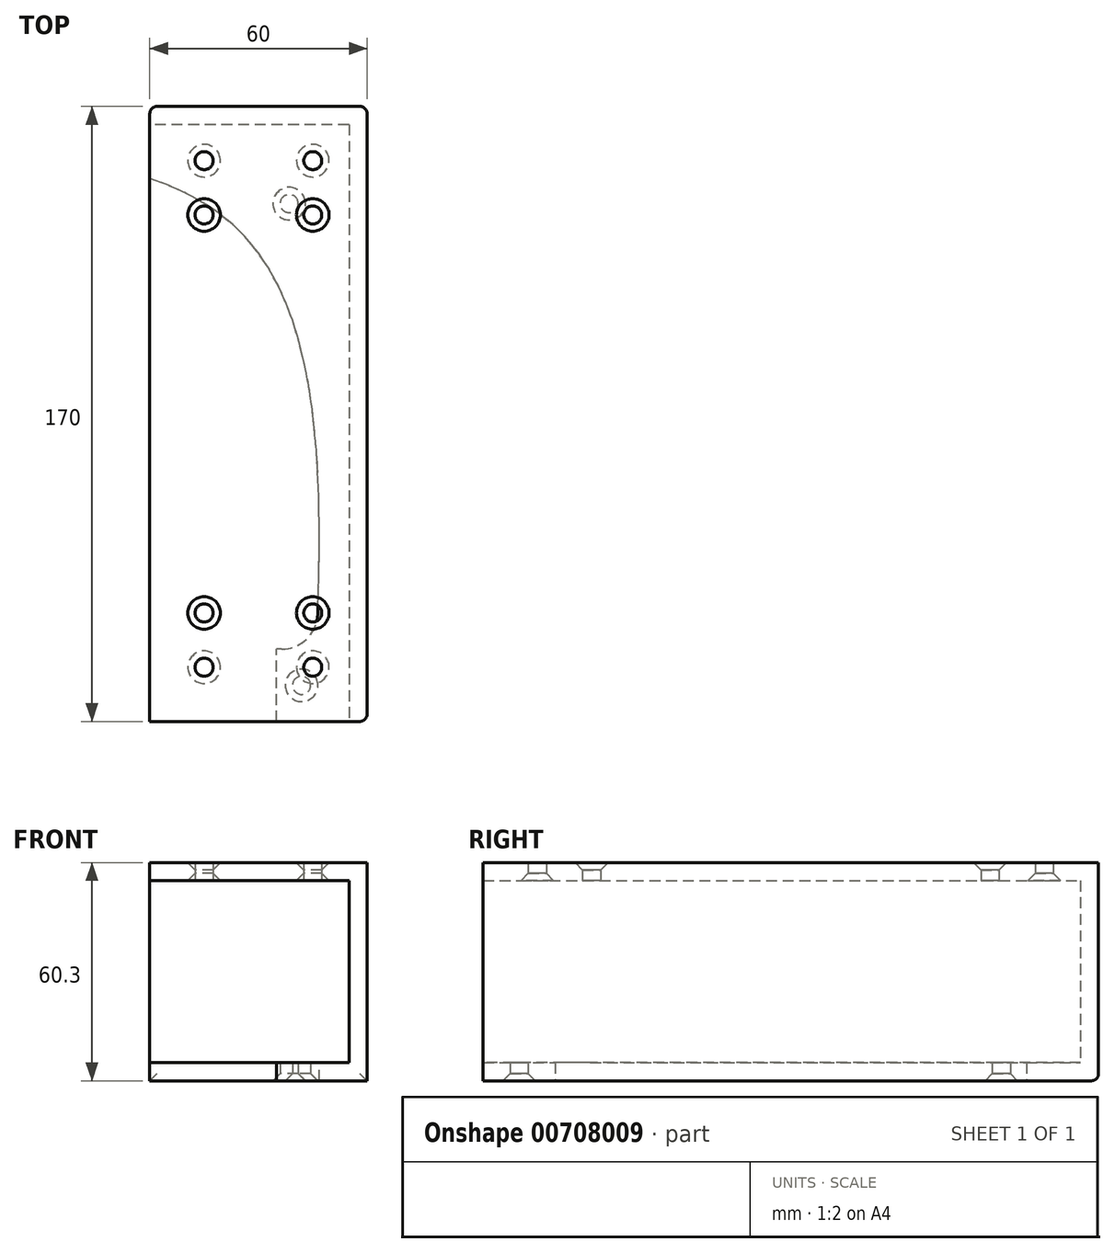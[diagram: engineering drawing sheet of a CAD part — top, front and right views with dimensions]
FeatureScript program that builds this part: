
annotation { "Feature Type Name" : "Feature", "Feature Type Description" : "" }
export const myFeature = defineFeature(function(context is Context, id is Id, definition is map)
    precondition{}
    {
        {
            var Q0;
            Q0=qCreatedBy(makeId("Top.planeOp"),FACE);
            var sketch = newSketch(context, id + "F0", { "sketchPlane" : qUnion([Q0])});
            skLineSegment(sketch, "E0.bottom", {"start": v(0, 0) * mm, "end": v(-60, 0) * mm});
            skLineSegment(sketch, "E0.top", {"start": v(0, 170) * mm, "end": v(-15, 170) * mm});
            skLineSegment(sketch, "E0.left", {"start": v(0, 0) * mm, "end": v(0, 170) * mm});
            skFitSpline(sketch, "E1", {"points": [v(-15, 170) * mm, v(-35.25, 34.39) * mm, v(-170, 15) * mm], "startDerivative": vector(17.06, -328.82) * mm, "endDerivative": vector(-327.27, 19.02) * mm});
            skCircle(sketch, "E2", {"center": v(-21.5, 26.87) * mm, "radius": 2.5 * mm});
            skCircle(sketch, "E3", {"center": v(-18.1, 160) * mm, "radius": 2.5 * mm});
            skLineSegment(sketch, "E4.bottom", {"start": v(0, 170) * mm, "end": v(-25, 170) * mm});
            skLineSegment(sketch, "E4.top", {"start": v(-23.62, 150) * mm, "end": v(-25, 150) * mm});
            skLineSegment(sketch, "E4.left", {"start": v(0, 170) * mm, "end": v(0, 150) * mm});
            skLineSegment(sketch, "E4.right", {"start": v(-25, 170) * mm, "end": v(-25, 150) * mm});
            skPoint(sketch, "E5.visualSharp", {"position": v(-150, 13.89) * mm});
            skPoint(sketch, "E6.visualSharp", {"position": v(-14.01, 150) * mm});
            skArc(sketch, "E6.filletArc", {"start": v(-13.62, 140.35) * mm, "mid": v(-16.67, 147.2) * mm, "end": v(-23.62, 150) * mm});
            skLineSegment(sketch, "E7", {"start": v(-60, 19.91) * mm, "end": v(-60, 0) * mm});
            skSolve(sketch);
        }
        {
            var Q0;
            Q0 = qSketchRegion(id + "F0", true);
            extrude(context, id + "F1", {"entities" : qUnion([Q0]), "depth" : 5 * mm, "offsetDistance" : 25 * mm});
        }
        {
            var Q0;
            Q0=makeQuery(id+"F1.opExtrude","SWEPT_FACE",FACE,{"disambiguationData":[OSD([sQuery(id+"F0.wireOp",EDGE,"E0.left")])]});
            var sketch = newSketch(context, id + "F2", { "sketchPlane" : qUnion([Q0])});
            skLineSegment(sketch, "E8.bottom", {"start": v(0, 5) * mm, "end": v(170, 5) * mm});
            skLineSegment(sketch, "E8.top", {"start": v(0, 55.3) * mm, "end": v(170, 55.3) * mm});
            skLineSegment(sketch, "E8.left", {"start": v(0, 5) * mm, "end": v(0, 55.3) * mm});
            skLineSegment(sketch, "E8.right", {"start": v(170, 5) * mm, "end": v(170, 55.3) * mm});
            skSolve(sketch);
        }
        {
            var Q0;
            Q0=makeQuery(id+"F2.imprint","IMPRINT",FACE,{"disambiguationData":[TD([[makeQuery(id+"F2.imprint","IMPRINT",EDGE,{"derivedFrom":sQuery(id+"F2.wireOp",EDGE,"E8.bottom")}),1.0]])]});
            extrude(context, id + "F3", {"entities" : qUnion([Q0]), "operationType" : NewBodyOperationType.ADD, "depth" : -5 * mm, "offsetDistance" : 25 * mm});
        }
        {
            var Q0;
            Q0=makeQuery(id+"F3.boolean.opBoolean","MERGE",FACE,{"derivedFrom":[makeQuery(id+"F1.opExtrude","SWEPT_FACE",FACE,{"disambiguationData":[OSD([sQuery(id+"F0.wireOp",EDGE,"E0.bottom")])]}),makeQuery(id+"F3.opExtrude","SWEPT_FACE",FACE,{"disambiguationData":[OSD([sQuery(id+"F2.wireOp",EDGE,"E8.left")])]})]});
            var sketch = newSketch(context, id + "F4", { "sketchPlane" : qUnion([Q0])});
            skLineSegment(sketch, "E9.bottom", {"start": v(-5, 5) * mm, "end": v(-60, 5) * mm});
            skLineSegment(sketch, "E9.top", {"start": v(-5, 55.3) * mm, "end": v(-60, 55.3) * mm});
            skLineSegment(sketch, "E9.left", {"start": v(-5, 5) * mm, "end": v(-5, 55.3) * mm});
            skLineSegment(sketch, "E10", {"start": v(-60, 55.3) * mm, "end": v(-60, 5) * mm});
            skSolve(sketch);
        }
        {
            var Q0;
            Q0 = qSketchRegion(id + "F4", true);
            extrude(context, id + "F5", {"entities" : qUnion([Q0]), "operationType" : NewBodyOperationType.ADD, "depth" : -5 * mm, "offsetDistance" : 25 * mm});
        }
        {
            var Q0;
            Q0=makeQuery(id+"F5.boolean.opBoolean","MERGE",FACE,{"derivedFrom":[makeQuery(id+"F3.opExtrude","SWEPT_FACE",FACE,{"disambiguationData":[OSD([sQuery(id+"F2.wireOp",EDGE,"E8.top")])]}),makeQuery(id+"F5.opExtrude","SWEPT_FACE",FACE,{"disambiguationData":[OSD([sQuery(id+"F4.wireOp",EDGE,"E9.top")])]})]});
            var sketch = newSketch(context, id + "F6", { "sketchPlane" : qUnion([Q0])});
            skLineSegment(sketch, "E11.bottom", {"start": v(0, 0) * mm, "end": v(-60, 0) * mm});
            skLineSegment(sketch, "E11.top", {"start": v(0, 170) * mm, "end": v(-60, 170) * mm});
            skLineSegment(sketch, "E11.left", {"start": v(0, 0) * mm, "end": v(0, 170) * mm});
            skLineSegment(sketch, "E11.right", {"start": v(-60, 0) * mm, "end": v(-60, 170) * mm});
            skSolve(sketch);
        }
        {
            var Q0;
            {var subQ4=sQuery(id+"F6.wireOp",EDGE,"E11.bottom");Q0=makeQuery(id+"F6.imprint","IMPRINT",FACE,{"disambiguationData":[TD([[makeQuery(id+"F6.imprint","IMPRINT",EDGE,{"derivedFrom":subQ4}),1.0]])]});}
            var sketch = newSketch(context, id + "F7", { "sketchPlane" : qUnion([Q0])});
            skLineSegment(sketch, "E12.bottom", {"start": v(0, 0) * mm, "end": v(-60, 0) * mm});
            skLineSegment(sketch, "E12.top", {"start": v(0, 170) * mm, "end": v(-60, 170) * mm});
            skLineSegment(sketch, "E12.left", {"start": v(0, 0) * mm, "end": v(0, 170) * mm});
            skLineSegment(sketch, "E12.right", {"start": v(-60, 0) * mm, "end": v(-60, 170) * mm});
            skLineSegment(sketch, "E13.bottom", {"start": v(0, 170) * mm, "end": v(-15, 170) * mm});
            skLineSegment(sketch, "E13.top", {"start": v(0, 155) * mm, "end": v(-15, 155) * mm, "construction": true});
            skLineSegment(sketch, "E13.left", {"start": v(0, 170) * mm, "end": v(0, 155) * mm});
            skLineSegment(sketch, "E13.right", {"start": v(-15, 170) * mm, "end": v(-15, 155) * mm, "construction": true});
            skLineSegment(sketch, "E14.bottom", {"start": v(0, 0) * mm, "end": v(-15, 0) * mm});
            skLineSegment(sketch, "E14.top", {"start": v(0, 15) * mm, "end": v(-15, 15) * mm, "construction": true});
            skLineSegment(sketch, "E14.left", {"start": v(0, 0) * mm, "end": v(0, 15) * mm});
            skLineSegment(sketch, "E14.right", {"start": v(-15, 0) * mm, "end": v(-15, 15) * mm, "construction": true});
            skLineSegment(sketch, "E15.bottom", {"start": v(-60, 0) * mm, "end": v(-45, 0) * mm});
            skLineSegment(sketch, "E15.top", {"start": v(-60, 15) * mm, "end": v(-45, 15) * mm, "construction": true});
            skLineSegment(sketch, "E15.left", {"start": v(-60, 0) * mm, "end": v(-60, 15) * mm});
            skLineSegment(sketch, "E15.right", {"start": v(-45, 0) * mm, "end": v(-45, 15) * mm, "construction": true});
            skLineSegment(sketch, "E16.bottom", {"start": v(-60, 170) * mm, "end": v(-45, 170) * mm});
            skLineSegment(sketch, "E16.top", {"start": v(-60, 155) * mm, "end": v(-45, 155) * mm, "construction": true});
            skLineSegment(sketch, "E16.left", {"start": v(-60, 170) * mm, "end": v(-60, 155) * mm});
            skLineSegment(sketch, "E16.right", {"start": v(-45, 170) * mm, "end": v(-45, 155) * mm, "construction": true});
            skCircle(sketch, "E17", {"center": v(-15, 155) * mm, "radius": 2.5 * mm});
            skCircle(sketch, "E18", {"center": v(-45, 155) * mm, "radius": 2.5 * mm});
            skCircle(sketch, "E19", {"center": v(-15, 15) * mm, "radius": 2.5 * mm});
            skCircle(sketch, "E20", {"center": v(-45, 15) * mm, "radius": 2.5 * mm});
            skLineSegment(sketch, "E21", {"start": v(-15, 15) * mm, "end": v(-15, 30) * mm, "construction": true});
            skLineSegment(sketch, "E22", {"start": v(-45, 15) * mm, "end": v(-45, 30) * mm, "construction": true});
            skLineSegment(sketch, "E23", {"start": v(-15, 155) * mm, "end": v(-15, 140) * mm, "construction": true});
            skLineSegment(sketch, "E24", {"start": v(-45, 155) * mm, "end": v(-45, 140) * mm, "construction": true});
            skCircle(sketch, "E25", {"center": v(-15, 140) * mm, "radius": 2.5 * mm});
            skCircle(sketch, "E26", {"center": v(-45, 140) * mm, "radius": 2.5 * mm});
            skCircle(sketch, "E27", {"center": v(-45, 30) * mm, "radius": 2.5 * mm});
            skCircle(sketch, "E28", {"center": v(-15, 30) * mm, "radius": 2.5 * mm});
            skSolve(sketch);
        }
        {
            var Q0;
            Q0 = qSketchRegion(id + "F7", true);
            extrude(context, id + "F8", {"entities" : qUnion([Q0]), "operationType" : NewBodyOperationType.ADD, "depth" : 5 * mm, "offsetDistance" : 25 * mm});
        }
        {
            var Q0;
            Q0=makeQuery(id+"F8.opExtrude","CAP_EDGE",EDGE,{"disambiguationData":[OSD([sQuery(id+"F7.wireOp",EDGE,"E25")])],"isStart":false});
            var Q1;
            Q1=makeQuery(id+"F8.opExtrude","CAP_EDGE",EDGE,{"disambiguationData":[OSD([sQuery(id+"F7.wireOp",EDGE,"E26")])],"isStart":false});
            var Q2;
            Q2=makeQuery(id+"F8.opExtrude","CAP_EDGE",EDGE,{"disambiguationData":[OSD([sQuery(id+"F7.wireOp",EDGE,"E28")])],"isStart":false});
            var Q3;
            Q3=makeQuery(id+"F8.opExtrude","CAP_EDGE",EDGE,{"disambiguationData":[OSD([sQuery(id+"F7.wireOp",EDGE,"E27")])],"isStart":false});
            chamfer(context, id + "F9", {"entities" : qUnion([Q0, Q1, Q2, Q3]), "width" : 2 * mm, "tangentPropagation" : true});
        }
        {
            var Q0;
            Q0=makeQuery(id+"F8.opExtrude","CAP_EDGE",EDGE,{"disambiguationData":[OSD([sQuery(id+"F7.wireOp",EDGE,"E18")])],"isStart":true});
            var Q1;
            Q1=makeQuery(id+"F8.opExtrude","CAP_EDGE",EDGE,{"disambiguationData":[OSD([sQuery(id+"F7.wireOp",EDGE,"E17")])],"isStart":true});
            var Q2;
            Q2=makeQuery(id+"F8.opExtrude","CAP_EDGE",EDGE,{"disambiguationData":[OSD([sQuery(id+"F7.wireOp",EDGE,"E20")])],"isStart":true});
            var Q3;
            Q3=makeQuery(id+"F8.opExtrude","CAP_EDGE",EDGE,{"disambiguationData":[OSD([sQuery(id+"F7.wireOp",EDGE,"E19")])],"isStart":true});
            chamfer(context, id + "F10", {"entities" : qUnion([Q0, Q1, Q2, Q3]), "width" : 2 * mm, "tangentPropagation" : true});
        }
        {
            var Q0;
            Q0=makeQuery(id+"F1.opExtrude","CAP_EDGE",EDGE,{"disambiguationData":[OSD([sQuery(id+"F0.wireOp",EDGE,"E2")])],"isStart":true});
            var Q1;
            Q1=makeQuery(id+"F1.opExtrude","CAP_EDGE",EDGE,{"disambiguationData":[OSD([sQuery(id+"F0.wireOp",EDGE,"E3")])],"isStart":true});
            var Q2;
            Q2=makeQuery(id+"F1.opExtrude","CAP_EDGE",EDGE,{"disambiguationData":[OSD([sQuery(id+"F0.wireOp",EDGE,"602ekmY3-djV7-0EYo-3G5f-2V9RUtqw9AcJ")])],"isStart":true});
            chamfer(context, id + "F11", {"entities" : qUnion([Q0, Q1, Q2]), "width" : 2 * mm, "tangentPropagation" : true});
        }
        {
            var Q0;
            Q0=makeQuery(id+"F8.boolean.opBoolean","MERGE",EDGE,{"derivedFrom":[makeQuery(id+"F3.boolean.opBoolean","MERGE",EDGE,{"derivedFrom":[makeQuery(id+"F1.opExtrude","SWEPT_EDGE",EDGE,{"disambiguationData":[OSD([sQuery(id+"F0.wireOp",EDGE,"E0.bottom"),sQuery(id+"F0.wireOp",EDGE,"E0.left")])]}),makeQuery(id+"F3.opExtrude","CAP_EDGE",EDGE,{"disambiguationData":[OSD([sQuery(id+"F2.wireOp",EDGE,"E8.left")])],"isStart":true})]}),makeQuery(id+"F8.opExtrude","SWEPT_EDGE",EDGE,{"disambiguationData":[OSD([sQuery(id+"F7.wireOp",EDGE,"E14.bottom"),sQuery(id+"F7.wireOp",EDGE,"E14.left")])]})]});
            var Q1;
            Q1=makeQuery(id+"F8.opExtrude","SWEPT_EDGE",EDGE,{"disambiguationData":[OSD([sQuery(id+"F7.wireOp",EDGE,"E15.bottom"),sQuery(id+"F7.wireOp",EDGE,"E15.left")])]});
            var Q2;
            Q2=makeQuery(id+"F5.opExtrude","CAP_EDGE",EDGE,{"disambiguationData":[OSD([sQuery(id+"F4.wireOp",EDGE,"uduKuWtT-cO4U-pCKe-B4Cu-s4ce6nYD45D1")])],"isStart":true});
            var Q3;
            Q3=makeQuery(id+"F5.boolean.opBoolean","MERGE",EDGE,{"derivedFrom":[makeQuery(id+"F1.opExtrude","SWEPT_EDGE",EDGE,{"disambiguationData":[OSD([sQuery(id+"F0.wireOp",EDGE,"E0.bottom"),sQuery(id+"F0.wireOp",EDGE,"OZDD4q5u-z9Ca-XiRg-jXSI-U4c8fKiU3yoC")])]}),makeQuery(id+"F5.opExtrude","CAP_EDGE",EDGE,{"disambiguationData":[OSD([sQuery(id+"F4.wireOp",EDGE,"E9.right")])],"isStart":true})]});
            var Q4;
            Q4=makeQuery(id+"F1.opExtrude","CAP_EDGE",EDGE,{"disambiguationData":[OSD([sQuery(id+"F0.wireOp",EDGE,"E0.bottom")])],"isStart":true});
            var Q5;
            Q5=makeQuery(id+"F8.boolean.opBoolean","MERGE",EDGE,{"derivedFrom":[makeQuery(id+"F3.boolean.opBoolean","MERGE",EDGE,{"derivedFrom":[makeQuery(id+"F1.opExtrude","SWEPT_EDGE",EDGE,{"disambiguationData":[OSD([sQuery(id+"F0.wireOp",EDGE,"E0.left"),sQuery(id+"F0.wireOp",EDGE,"E0.top")])]}),makeQuery(id+"F3.opExtrude","CAP_EDGE",EDGE,{"disambiguationData":[OSD([sQuery(id+"F2.wireOp",EDGE,"E8.right")])],"isStart":true})]}),makeQuery(id+"F8.opExtrude","SWEPT_EDGE",EDGE,{"disambiguationData":[OSD([sQuery(id+"F7.wireOp",EDGE,"E13.bottom"),sQuery(id+"F7.wireOp",EDGE,"E13.left")])]})]});
            var Q6;
            Q6=makeQuery(id+"F8.opExtrude","SWEPT_EDGE",EDGE,{"disambiguationData":[OSD([sQuery(id+"F7.wireOp",EDGE,"E16.bottom"),sQuery(id+"F7.wireOp",EDGE,"E16.left")])]});
            fillet(context, id + "F12", {"entities" : qUnion([Q0, Q1, Q2, Q3, Q4, Q5, Q6]), "radius" : 2 * mm, "tangentPropagation" : true, "allowEdgeOverflow" : false});
        }
        {
            var Q0;
            Q0=makeQuery(id+"F1.opExtrude","SWEPT_BODY",BODY,{"disambiguationData":[OSD([sQuery(id+"F0.wireOp",EDGE,"E0.bottom"),sQuery(id+"F0.wireOp",EDGE,"E0.left"),sQuery(id+"F0.wireOp",EDGE,"E1"),sQuery(id+"F0.wireOp",EDGE,"E2"),sQuery(id+"F0.wireOp",EDGE,"E3"),sQuery(id+"F0.wireOp",EDGE,"E4.bottom"),sQuery(id+"F0.wireOp",EDGE,"E4.top"),sQuery(id+"F0.wireOp",EDGE,"E4.left"),sQuery(id+"F0.wireOp",EDGE,"E4.right"),sQuery(id+"F0.wireOp",EDGE,"E6.filletArc"),sQuery(id+"F0.wireOp",EDGE,"E7")])]});
            var Q1;
            Q1=makeQuery(id+"F8.boolean.opBoolean","MERGE",FACE,{"derivedFrom":[makeQuery(id+"F5.boolean.opBoolean","MERGE",FACE,{"derivedFrom":[makeQuery(id+"F3.boolean.opBoolean","MERGE",FACE,{"derivedFrom":[makeQuery(id+"F1.opExtrude","SWEPT_FACE",FACE,{"disambiguationData":[OSD([sQuery(id+"F0.wireOp",EDGE,"E0.bottom")])]}),makeQuery(id+"F3.opExtrude","SWEPT_FACE",FACE,{"disambiguationData":[OSD([sQuery(id+"F2.wireOp",EDGE,"E8.left")])]})]}),makeQuery(id+"F5.opExtrude","CAP_FACE",FACE,{"disambiguationData":[OSD([sQuery(id+"F4.wireOp",EDGE,"E9.bottom"),sQuery(id+"F4.wireOp",EDGE,"E9.left"),sQuery(id+"F4.wireOp",EDGE,"E9.top"),sQuery(id+"F4.wireOp",EDGE,"E10")])],"isStart":true})]}),makeQuery(id+"F8.opExtrude","SWEPT_FACE",FACE,{"disambiguationData":[OSD([sQuery(id+"F7.wireOp",EDGE,"E12.bottom"),sQuery(id+"F7.wireOp",EDGE,"E14.bottom"),sQuery(id+"F7.wireOp",EDGE,"E15.bottom")])]})]});
            mirror(context, id + "F13", {"entities" : qUnion([Q0]), "mirrorPlane" : qUnion([Q1])});
        }
        {
            var Q0;
            Q0=makeQuery(id+"F1.opExtrude","SWEPT_BODY",BODY,{"disambiguationData":[OSD([sQuery(id+"F0.wireOp",EDGE,"E0.bottom"),sQuery(id+"F0.wireOp",EDGE,"E0.left"),sQuery(id+"F0.wireOp",EDGE,"E1"),sQuery(id+"F0.wireOp",EDGE,"E2"),sQuery(id+"F0.wireOp",EDGE,"E3"),sQuery(id+"F0.wireOp",EDGE,"E4.bottom"),sQuery(id+"F0.wireOp",EDGE,"E4.top"),sQuery(id+"F0.wireOp",EDGE,"E4.left"),sQuery(id+"F0.wireOp",EDGE,"E4.right"),sQuery(id+"F0.wireOp",EDGE,"E6.filletArc"),sQuery(id+"F0.wireOp",EDGE,"E7")])]});
            deleteBodies(context, id + "F14", {"entities" : qUnion([Q0])});
        }
    });
